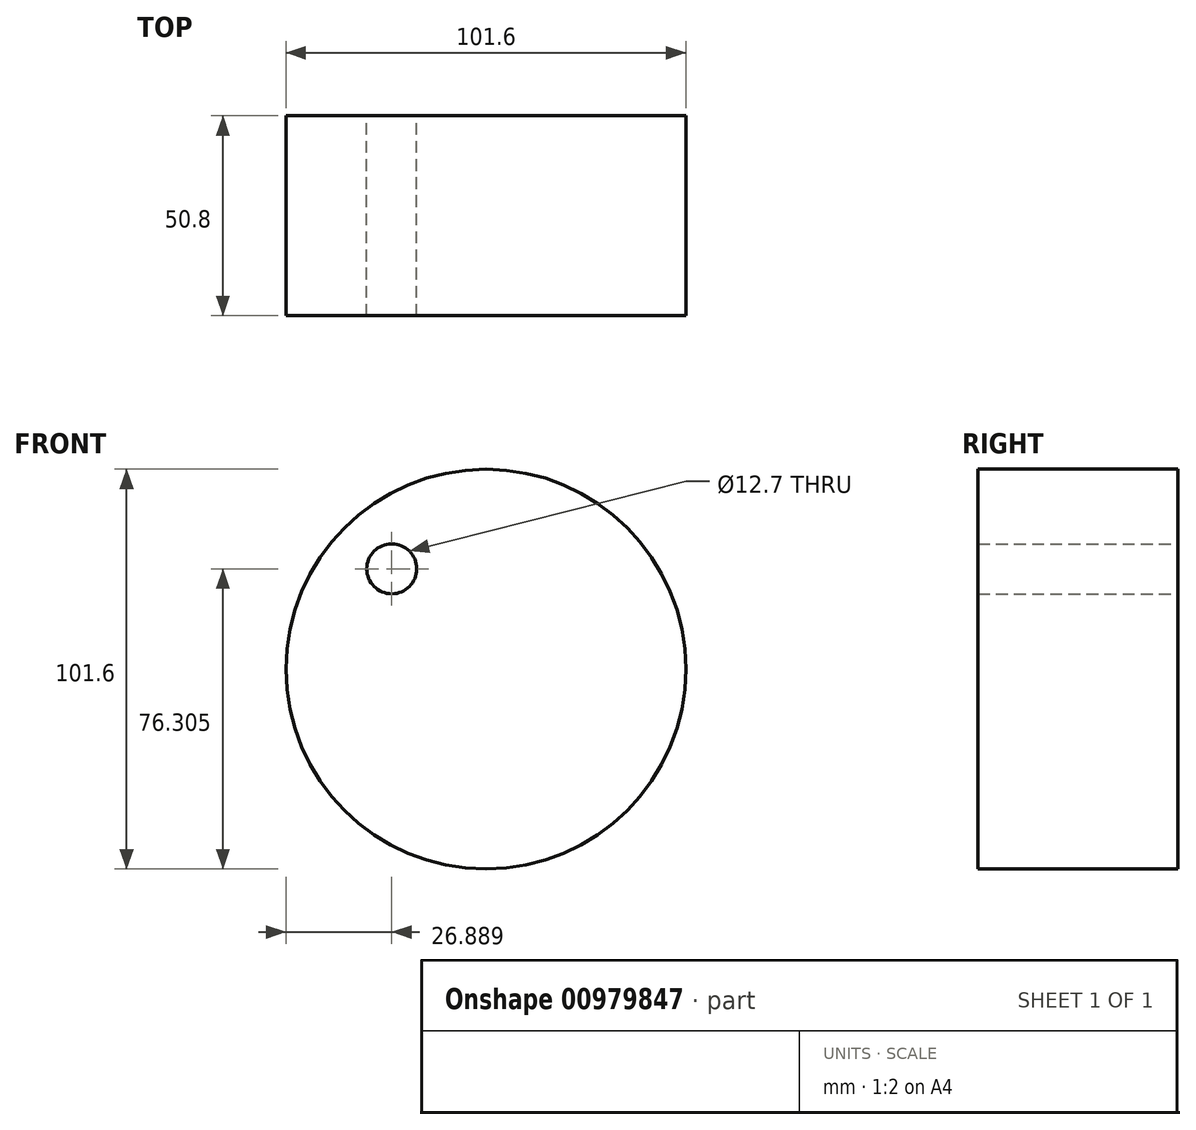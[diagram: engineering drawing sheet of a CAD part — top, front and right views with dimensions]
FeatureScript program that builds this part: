
annotation { "Feature Type Name" : "Feature", "Feature Type Description" : "" }
export const myFeature = defineFeature(function(context is Context, id is Id, definition is map)
    precondition{}
    {
        {
            var Q0;
            Q0=qCreatedBy(makeId("Front.planeOp"),FACE);
            var sketch = newSketch(context, id + "F0", { "sketchPlane" : qUnion([Q0])});
            skCircle(sketch, "E0", {"center": v(0, 0) * mm, "radius": 50.8 * mm});
            skCircle(sketch, "E1", {"center": v(-23.91, 25.5) * mm, "radius": 6.35 * mm});
            skSolve(sketch);
        }
        {
            var Q0;
            Q0 = qSketchRegion(id + "F0", true);
            extrude(context, id + "F1", {"entities" : qUnion([Q0]), "depth" : 25.4 * mm, "offsetDistance" : 25.4 * mm});
        }
        {
            var Q0;
            Q0=makeQuery(id+"F1.opExtrude","CAP_FACE",FACE,{"disambiguationData":[OSD([sQuery(id+"F0.wireOp",EDGE,"E0"),sQuery(id+"F0.wireOp",EDGE,"E1")])],"isStart":false});
            extrude(context, id + "F2", {"entities" : qUnion([Q0]), "operationType" : NewBodyOperationType.ADD, "depth" : 25.4 * mm, "offsetDistance" : 25.4 * mm});
        }
    });
